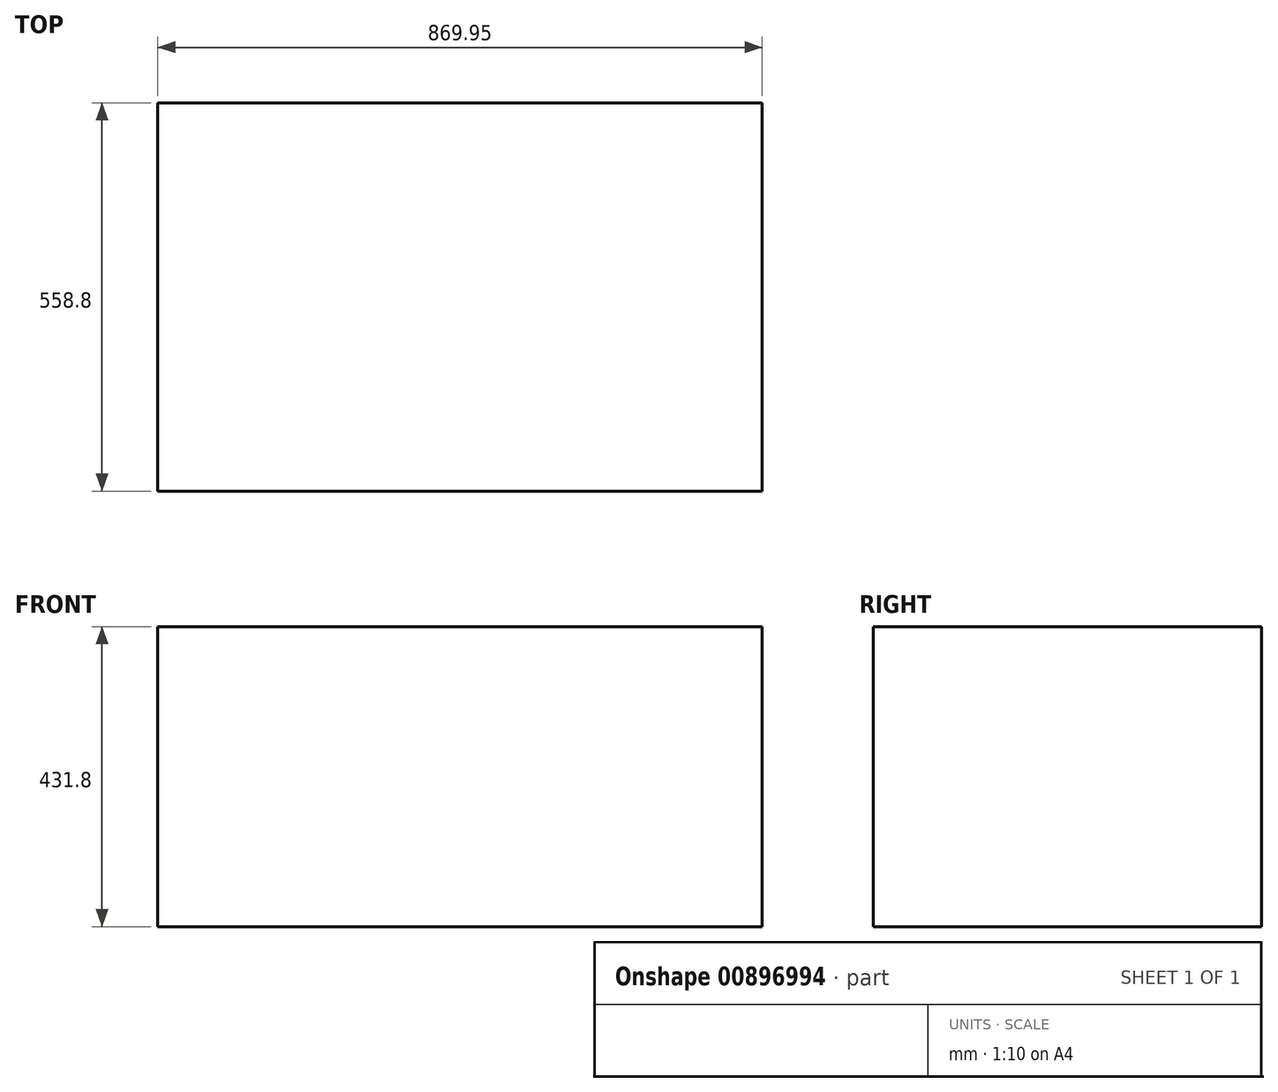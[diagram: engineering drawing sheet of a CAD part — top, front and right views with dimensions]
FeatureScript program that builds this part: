
annotation { "Feature Type Name" : "Feature", "Feature Type Description" : "" }
export const myFeature = defineFeature(function(context is Context, id is Id, definition is map)
    precondition{}
    {
        {
            var Q0;
            Q0=qCreatedBy(makeId("Top.planeOp"),FACE);
            var sketch = newSketch(context, id + "F0", { "sketchPlane" : qUnion([Q0])});
            skLineSegment(sketch, "E0.bottom", {"start": v(41.3, 0) * mm, "end": v(911.24, 0) * mm});
            skLineSegment(sketch, "E0.top", {"start": v(41.3, 558.8) * mm, "end": v(911.24, 558.8) * mm});
            skLineSegment(sketch, "E0.left", {"start": v(41.3, 0) * mm, "end": v(41.3, 558.8) * mm});
            skLineSegment(sketch, "E0.right", {"start": v(911.24, 0) * mm, "end": v(911.24, 558.8) * mm});
            skSolve(sketch);
        }
        {
            var Q0;
            Q0 = qSketchRegion(id + "F0", true);
            extrude(context, id + "F1", {"entities" : qUnion([Q0]), "depth" : 431.8 * mm, "offsetDistance" : 25.4 * mm});
        }
    });
